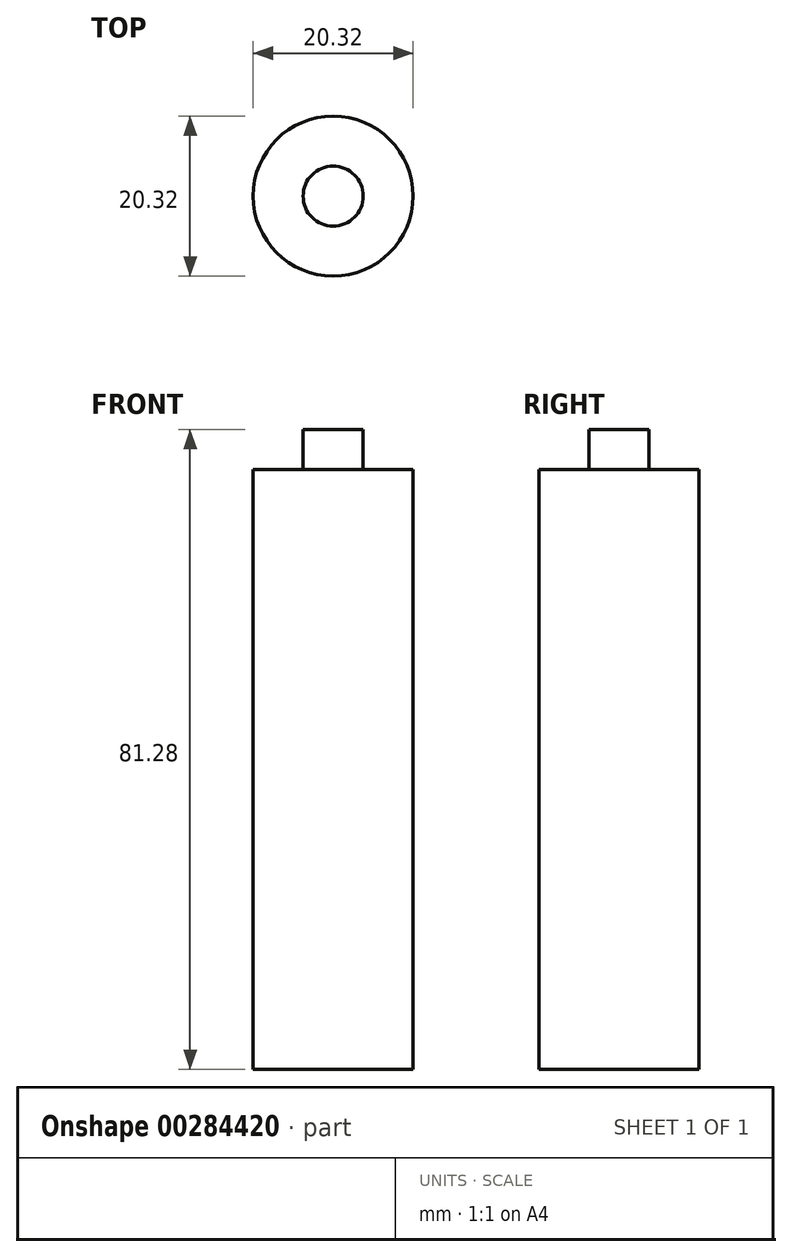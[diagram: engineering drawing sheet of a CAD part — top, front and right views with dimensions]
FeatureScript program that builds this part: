
annotation { "Feature Type Name" : "Feature", "Feature Type Description" : "" }
export const myFeature = defineFeature(function(context is Context, id is Id, definition is map)
    precondition{}
    {
        {
            var Q0;
            Q0=qCreatedBy(makeId("Front.planeOp"),FACE);
            var sketch = newSketch(context, id + "F0", { "sketchPlane" : qUnion([Q0])});
            skLineSegment(sketch, "E0", {"start": v(0, 49.84) * mm, "end": v(0, -50.1) * mm, "construction": true});
            skLineSegment(sketch, "E1.bottom", {"start": v(-10.16, 35.14) * mm, "end": v(0, 35.14) * mm});
            skLineSegment(sketch, "E1.top", {"start": v(-10.16, -41.06) * mm, "end": v(0, -41.06) * mm});
            skLineSegment(sketch, "E1.left", {"start": v(-10.16, 35.14) * mm, "end": v(-10.16, -41.06) * mm});
            skLineSegment(sketch, "E1.right", {"start": v(0, 35.14) * mm, "end": v(0, -41.06) * mm});
            skLineSegment(sketch, "E2.bottom", {"start": v(-3.8, 40.22) * mm, "end": v(0, 40.22) * mm});
            skLineSegment(sketch, "E2.top", {"start": v(-3.8, 35.14) * mm, "end": v(0, 35.14) * mm});
            skLineSegment(sketch, "E2.left", {"start": v(-3.8, 40.22) * mm, "end": v(-3.8, 35.14) * mm});
            skLineSegment(sketch, "E2.right", {"start": v(0, 40.22) * mm, "end": v(0, 35.14) * mm});
            skSolve(sketch);
        }
        {
            var Q0;
            Q0 = qSketchRegion(id + "F0", true);
            var Q1;
            Q1=sQuery(id+"F0.wireOp",EDGE,"E2.right");
            revolve(context, id + "F1", {"entities" : qUnion([Q0]), "axis" : qUnion([Q1]), "revolveType" : RevolveType.FULL});
        }
    });
